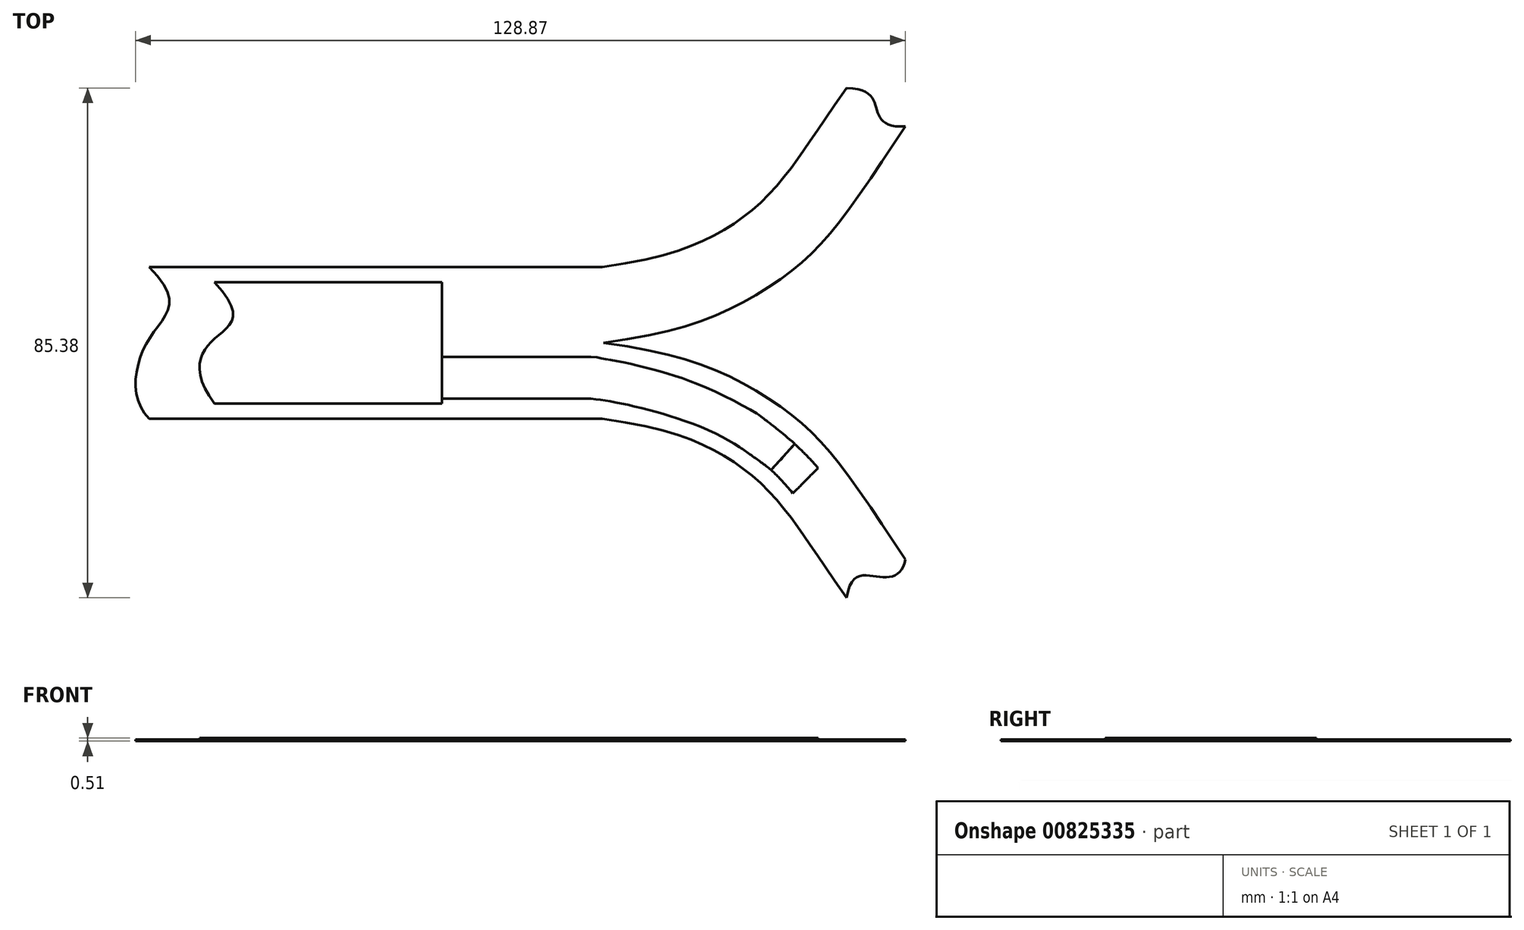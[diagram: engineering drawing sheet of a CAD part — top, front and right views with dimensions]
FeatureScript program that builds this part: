
annotation { "Feature Type Name" : "Feature", "Feature Type Description" : "" }
export const myFeature = defineFeature(function(context is Context, id is Id, definition is map)
    precondition{}
    {
        {
            var Q0;
            Q0=qCreatedBy(makeId("Top.planeOp"),FACE);
            var sketch = newSketch(context, id + "F0", { "sketchPlane" : qUnion([Q0])});
            skLineSegment(sketch, "E0.bottom", {"start": v(0, 0) * mm, "end": v(75.88, 0) * mm});
            skLineSegment(sketch, "E0.top", {"start": v(0, -25.4) * mm, "end": v(75.88, -25.4) * mm});
            skFitSpline(sketch, "E1", {"points": [v(76.09, -12.7) * mm, v(96.13, -7.56) * mm, v(107, -1.09) * mm, v(114.72, 6.43) * mm, v(126.62, 23.55) * mm], "startDerivative": vector(97.2, 13.4) * mm, "endDerivative": vector(47, 70.5) * mm});
            skFitSpline(sketch, "E2", {"points": [v(0, 0) * mm, v(0, -12.06) * mm, v(0, -25.4) * mm], "startDerivative": vector(38.65, -37.27) * mm, "endDerivative": vector(20.12, -20.39) * mm});
            skFitSpline(sketch, "E3", {"points": [v(75.88, 0) * mm, v(94.67, 5.35) * mm, v(102.4, 10.78) * mm, v(108.45, 17.88) * mm, v(116.8, 29.99) * mm], "startDerivative": vector(97.2, 13.4) * mm, "endDerivative": vector(49.33, 70.47) * mm});
            skFitSpline(sketch, "E4.MirrorCS", {"points": [v(76.09, -12.7) * mm, v(96.13, -17.84) * mm, v(107, -24.31) * mm, v(114.72, -31.83) * mm, v(126.62, -48.95) * mm], "startDerivative": vector(97.2, -13.4) * mm, "endDerivative": vector(47, -70.5) * mm});
            skFitSpline(sketch, "E5.MirrorCS", {"points": [v(75.88, -25.4) * mm, v(94.67, -30.75) * mm, v(102.4, -36.18) * mm, v(108.45, -43.28) * mm, v(116.8, -55.39) * mm], "startDerivative": vector(97.2, -13.4) * mm, "endDerivative": vector(49.33, -70.47) * mm});
            skFitSpline(sketch, "E6", {"points": [v(116.8, 29.99) * mm, v(121.86, 26.36) * mm, v(126.62, 23.55) * mm], "startDerivative": vector(25.47, -0.98) * mm, "endDerivative": vector(21.47, 1.57) * mm});
            skFitSpline(sketch, "E7", {"points": [v(116.8, -55.39) * mm, v(122.52, -51.92) * mm, v(126.62, -48.95) * mm], "startDerivative": vector(4.39, 27.77) * mm, "endDerivative": vector(2.37, 16.65) * mm});
            skSolve(sketch);
        }
        {
            var Q0;
            Q0=makeQuery(id+"F0.imprint","IMPRINT",FACE,{"disambiguationData":[TD([[makeQuery(id+"F0.imprint","IMPRINT",EDGE,{"derivedFrom":sQuery(id+"F0.wireOp",EDGE,"E0.bottom")}),-1.0]])]});
            extrude(context, id + "F1", {"entities" : qUnion([Q0]), "depth" : 0.25 * mm, "offsetDistance" : 25.4 * mm});
        }
        {
            var Q0;
            Q0=makeQuery(id+"F1.opExtrude","CAP_FACE",FACE,{"disambiguationData":[OSD([sQuery(id+"F0.wireOp",EDGE,"E0.bottom"),sQuery(id+"F0.wireOp",EDGE,"E0.top"),sQuery(id+"F0.wireOp",EDGE,"22a7fe5c-ccfa-4618-8f4b-4832fbfde12b"),sQuery(id+"F0.wireOp",EDGE,"277a3f10-a1f8-449c-afc6-e7f7526abaa40.MirrorCS"),sQuery(id+"F0.wireOp",EDGE,"E1"),sQuery(id+"F0.wireOp",EDGE,"b417c2f6-0d06-425d-9e04-0dbbccb093a60.MirrorCS"),sQuery(id+"F0.wireOp",EDGE,"00d841b0-e8ac-4c99-8037-971bd440aa43"),sQuery(id+"F0.wireOp",EDGE,"d09ba595-feb1-45ed-8751-bb9a11bfb4f8"),sQuery(id+"F0.wireOp",EDGE,"E2")])],"isStart":false});
            var sketch = newSketch(context, id + "F2", { "sketchPlane" : qUnion([Q0])});
            skLineSegment(sketch, "E8", {"start": v(10.92, -2.54) * mm, "end": v(49.02, -2.54) * mm});
            skLineSegment(sketch, "E9", {"start": v(49.02, -2.54) * mm, "end": v(49.02, -22.86) * mm});
            skLineSegment(sketch, "E10", {"start": v(49.02, -22.86) * mm, "end": v(10.92, -22.86) * mm});
            skFitSpline(sketch, "E11", {"points": [v(10.92, -2.54) * mm, v(10.92, -12.04) * mm, v(10.92, -22.86) * mm], "startDerivative": vector(35.32, -36.98) * mm, "endDerivative": vector(23.17, -31.49) * mm});
            skSolve(sketch);
        }
        {
            var Q0;
            Q0=makeQuery(id+"F2.imprint","IMPRINT",FACE,{"disambiguationData":[TD([[makeQuery(id+"F2.imprint","IMPRINT",EDGE,{"derivedFrom":sQuery(id+"F2.wireOp",EDGE,"E8")}),-1.0]])]});
            extrude(context, id + "F3", {"entities" : qUnion([Q0]), "depth" : 0.25 * mm, "offsetDistance" : 25.4 * mm});
        }
        {
            var Q0;
            Q0=makeQuery(id+"F1.opExtrude","CAP_FACE",FACE,{"disambiguationData":[OSD([sQuery(id+"F0.wireOp",EDGE,"E0.bottom"),sQuery(id+"F0.wireOp",EDGE,"E0.top"),sQuery(id+"F0.wireOp",EDGE,"22a7fe5c-ccfa-4618-8f4b-4832fbfde12b"),sQuery(id+"F0.wireOp",EDGE,"277a3f10-a1f8-449c-afc6-e7f7526abaa40.MirrorCS"),sQuery(id+"F0.wireOp",EDGE,"E1"),sQuery(id+"F0.wireOp",EDGE,"b417c2f6-0d06-425d-9e04-0dbbccb093a60.MirrorCS"),sQuery(id+"F0.wireOp",EDGE,"00d841b0-e8ac-4c99-8037-971bd440aa43"),sQuery(id+"F0.wireOp",EDGE,"d09ba595-feb1-45ed-8751-bb9a11bfb4f8"),sQuery(id+"F0.wireOp",EDGE,"E2")])],"isStart":false});
            var sketch = newSketch(context, id + "F4", { "sketchPlane" : qUnion([Q0])});
            skLineSegment(sketch, "E12.left", {"start": v(49.04, -22.01) * mm, "end": v(49.04, -15.04) * mm});
            skLineSegment(sketch, "E13", {"start": v(49.04, -15.04) * mm, "end": v(74.03, -15.04) * mm});
            skLineSegment(sketch, "E14", {"start": v(49.04, -22.01) * mm, "end": v(74.03, -22.01) * mm});
            skFitSpline(sketch, "E15", {"points": [v(74.03, -22.01) * mm, v(76.2, -22.34) * mm, v(78.88, -22.8) * mm, v(83.67, -23.94) * mm, v(88.66, -25.4) * mm, v(94.83, -27.84) * mm, v(98.92, -30.16) * mm], "startDerivative": vector(18, -2.76) * mm, "endDerivative": vector(21.58, -13.36) * mm});
            skFitSpline(sketch, "E16", {"points": [v(74.03, -15.04) * mm, v(76.2, -15.37) * mm, v(78.88, -15.83) * mm, v(83.67, -16.97) * mm, v(88.66, -18.42) * mm, v(94.83, -20.87) * mm, v(101.76, -24.54) * mm], "startDerivative": vector(28.88, -1.55) * mm, "endDerivative": vector(21.58, -13.36) * mm});
            skFitSpline(sketch, "E17", {"points": [v(98.92, -30.16) * mm, v(101.76, -32.17) * mm, v(104.17, -34) * mm], "startDerivative": vector(5.62, -3.82) * mm, "endDerivative": vector(4.37, -3.87) * mm});
            skFitSpline(sketch, "E18", {"points": [v(101.76, -24.54) * mm, v(104.17, -26.34) * mm, v(108.12, -29.62) * mm], "startDerivative": vector(8.46, -5.95) * mm, "endDerivative": vector(10.2, -9.19) * mm});
            skFitSpline(sketch, "E19", {"points": [v(104.17, -34) * mm, v(106.19, -31.8) * mm, v(108.12, -29.62) * mm], "startDerivative": vector(4.06, 4.37) * mm, "endDerivative": vector(3.84, 4.4) * mm});
            skSolve(sketch);
        }
        {
            var Q0;
            Q0 = qSketchRegion(id + "F4", true);
            extrude(context, id + "F5", {"entities" : qUnion([Q0]), "depth" : 0.25 * mm, "offsetDistance" : 25.4 * mm});
        }
        {
            var Q0;
            Q0=makeQuery(id+"F1.opExtrude","CAP_FACE",FACE,{"disambiguationData":[OSD([sQuery(id+"F0.wireOp",EDGE,"E0.bottom"),sQuery(id+"F0.wireOp",EDGE,"E0.top"),sQuery(id+"F0.wireOp",EDGE,"E1"),sQuery(id+"F0.wireOp",EDGE,"E2"),sQuery(id+"F0.wireOp",EDGE,"E3"),sQuery(id+"F0.wireOp",EDGE,"E4.MirrorCS"),sQuery(id+"F0.wireOp",EDGE,"E5.MirrorCS"),sQuery(id+"F0.wireOp",EDGE,"E6"),sQuery(id+"F0.wireOp",EDGE,"E7")])],"isStart":false});
            var sketch = newSketch(context, id + "F6", { "sketchPlane" : qUnion([Q0])});
            skFitSpline(sketch, "E20", {"points": [v(104.17, -34) * mm, v(108.11, -29.64) * mm], "startDerivative": vector(3.95, 4.36) * mm, "endDerivative": vector(3.95, 4.36) * mm});
            skFitSpline(sketch, "E21", {"points": [v(104.17, -34) * mm, v(104.83, -34.63) * mm, v(105.54, -35.33) * mm, v(106.23, -36.1) * mm, v(106.86, -36.8) * mm, v(107.8, -37.9) * mm], "startDerivative": vector(3.84, -3.18) * mm, "endDerivative": vector(5.29, -6.74) * mm});
            skFitSpline(sketch, "E22", {"points": [v(107.8, -37.9) * mm, v(111.69, -34) * mm], "startDerivative": vector(4.54, 4.3) * mm, "endDerivative": vector(4.54, 4.3) * mm});
            skFitSpline(sketch, "E23", {"points": [v(108.11, -29.64) * mm, v(109.12, -30.58) * mm, v(110.04, -31.5) * mm, v(111.01, -32.52) * mm, v(112.05, -33.65) * mm], "startDerivative": vector(4.12, -3.8) * mm, "endDerivative": vector(3.97, -4.37) * mm});
            skFitSpline(sketch, "E24", {"points": [v(112.05, -33.65) * mm, v(111.69, -34) * mm], "startDerivative": vector(-0.36, -0.35) * mm, "endDerivative": vector(-0.36, -0.35) * mm});
            skSolve(sketch);
        }
        {
            var Q0;
            Q0 = qSketchRegion(id + "F6", true);
            extrude(context, id + "F7", {"entities" : qUnion([Q0]), "depth" : 0.25 * mm, "offsetDistance" : 25.4 * mm});
        }
    });
